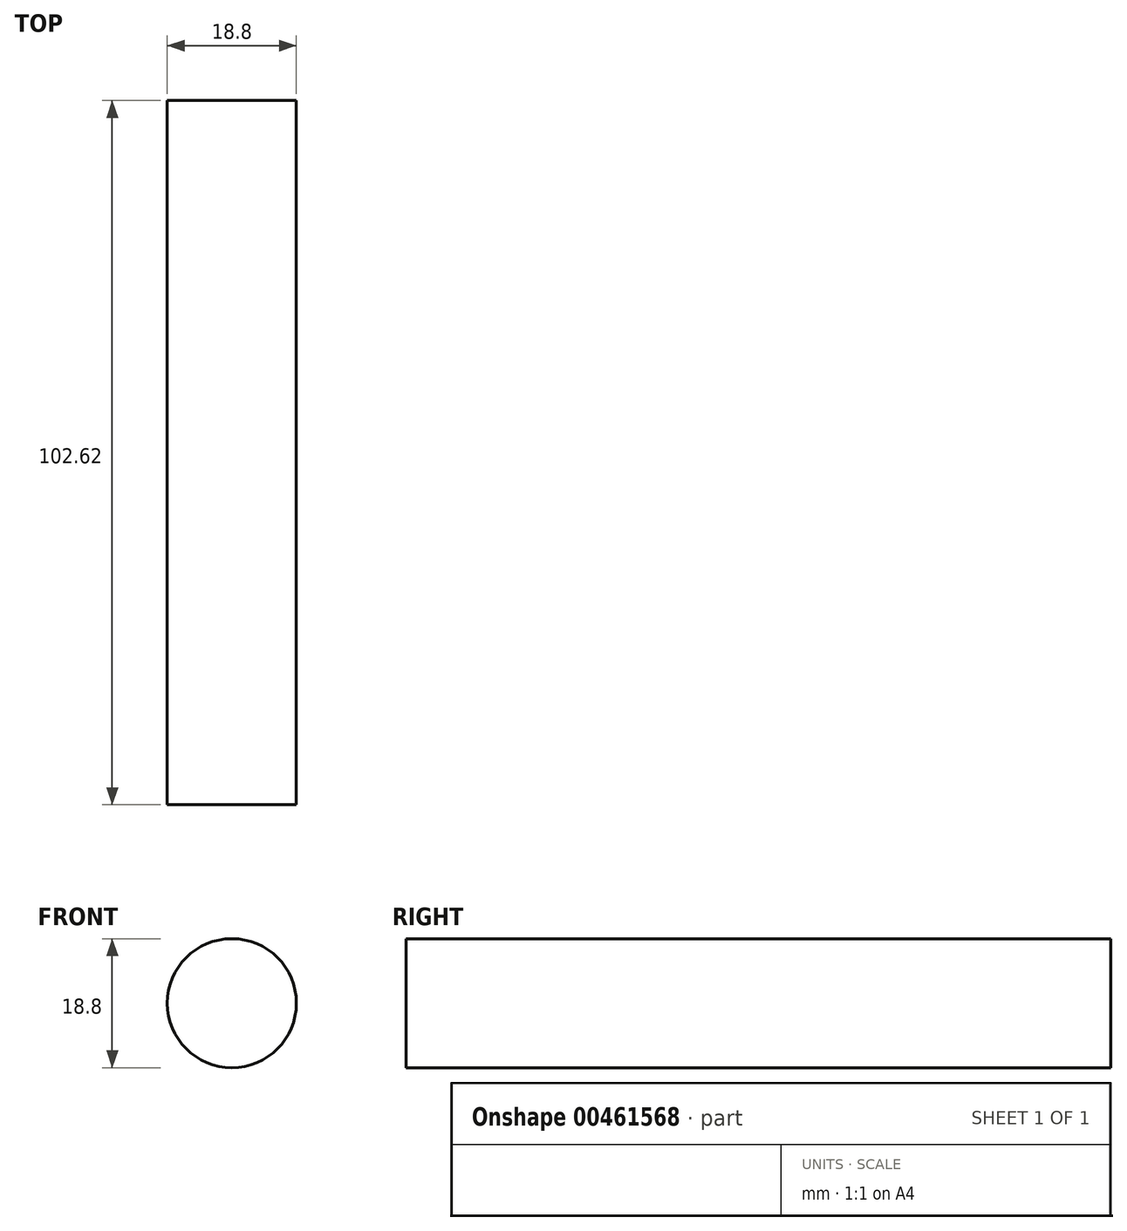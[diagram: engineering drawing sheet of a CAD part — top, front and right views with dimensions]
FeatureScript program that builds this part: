
annotation { "Feature Type Name" : "Feature", "Feature Type Description" : "" }
export const myFeature = defineFeature(function(context is Context, id is Id, definition is map)
    precondition{}
    {
        {
            var Q0;
            Q0=qCreatedBy(makeId("Front.planeOp"),FACE);
            var sketch = newSketch(context, id + "F0", { "sketchPlane" : qUnion([Q0])});
            skCircle(sketch, "E0", {"center": v(0, 0) * mm, "radius": 9.4 * mm});
            skSolve(sketch);
        }
        {
            var Q0;
            Q0=makeQuery(id+"F0.imprint","IMPRINT",FACE,{"disambiguationData":[TD([[makeQuery(id+"F0.imprint","IMPRINT",EDGE,{"derivedFrom":sQuery(id+"F0.wireOp",EDGE,"E0")}),1.0]])]});
            extrude(context, id + "F1", {"entities" : qUnion([Q0]), "depth" : 102.62 * mm});
        }
    });
